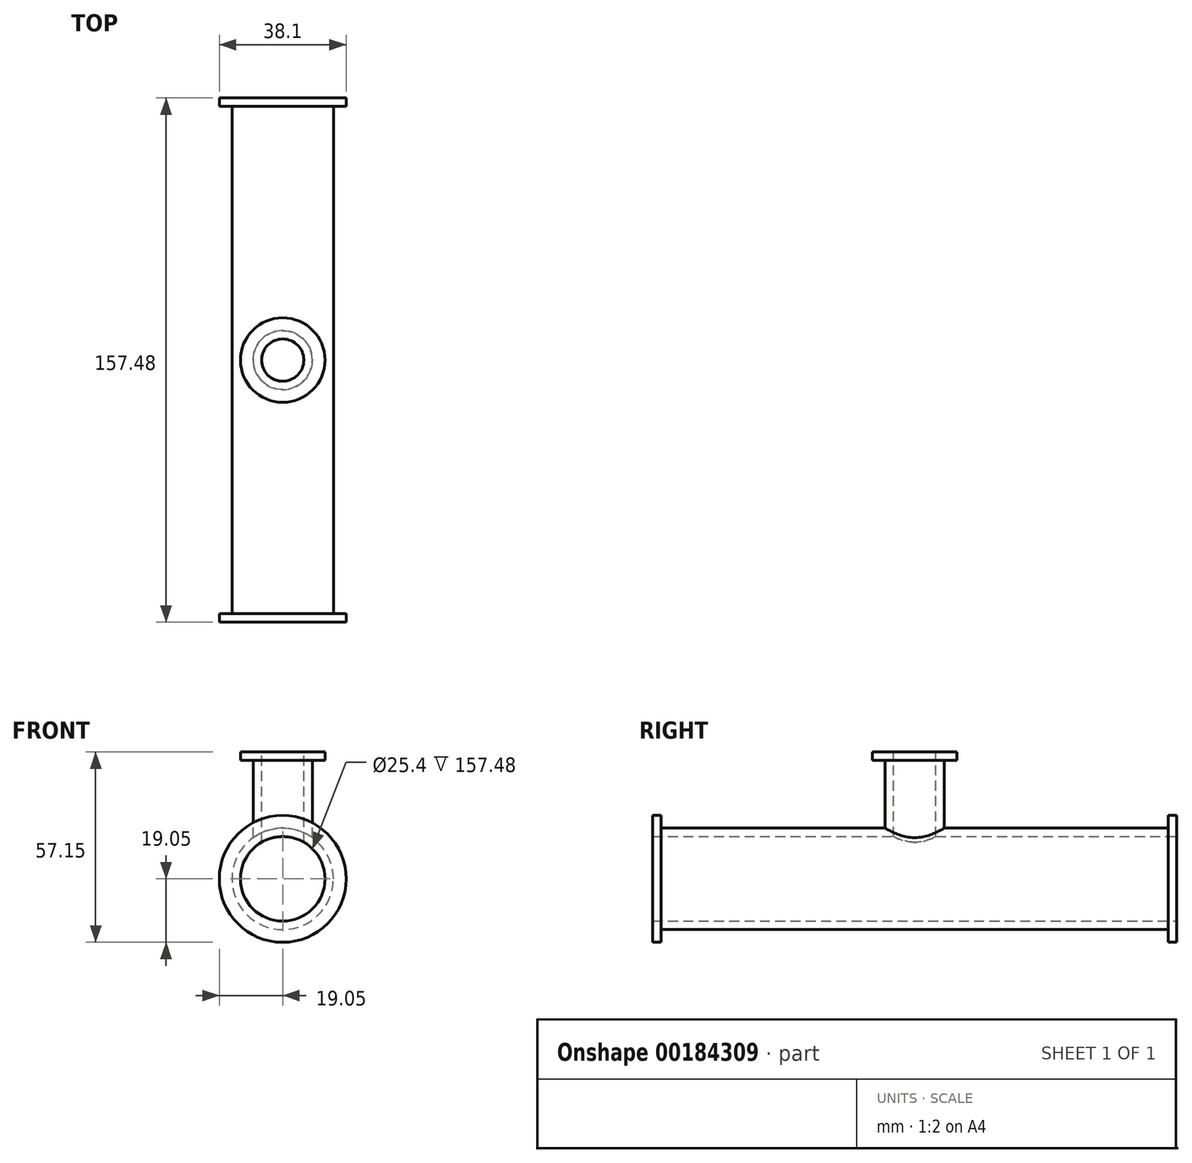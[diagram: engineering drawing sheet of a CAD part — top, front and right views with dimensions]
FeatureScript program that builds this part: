
annotation { "Feature Type Name" : "Feature", "Feature Type Description" : "" }
export const myFeature = defineFeature(function(context is Context, id is Id, definition is map)
    precondition{}
    {
        {
            var Q0;
            Q0=qCreatedBy(makeId("Front.planeOp"),FACE);
            var sketch = newSketch(context, id + "F0", { "sketchPlane" : qUnion([Q0])});
            skCircle(sketch, "E0", {"center": v(0, 0) * mm, "radius": 19.05 * mm});
            skCircle(sketch, "E1", {"center": v(0, 0) * mm, "radius": 12.7 * mm});
            skCircle(sketch, "E2", {"center": v(0, 0) * mm, "radius": 15.24 * mm});
            skSolve(sketch);
        }
        {
            var Q0;
            Q0=makeQuery(id+"F0.imprint","IMPRINT",FACE,{"disambiguationData":[TD([[makeQuery(id+"F0.imprint","IMPRINT",EDGE,{"derivedFrom":sQuery(id+"F0.wireOp",EDGE,"E1")}),-1.0]])]});
            extrude(context, id + "F1", {"entities" : qUnion([Q0]), "depth" : 157.48 * mm});
        }
        {
            var Q0;
            Q0=makeQuery(id+"F0.imprint","IMPRINT",FACE,{"disambiguationData":[TD([[makeQuery(id+"F0.imprint","IMPRINT",EDGE,{"derivedFrom":sQuery(id+"F0.wireOp",EDGE,"E0")}),1.0]])]});
            extrude(context, id + "F2", {"entities" : qUnion([Q0]), "operationType" : NewBodyOperationType.ADD, "depth" : 2.54 * mm});
        }
        {
            var Q0;
            Q0=makeQuery(id+"F1.opExtrude","CAP_FACE",FACE,{"disambiguationData":[OSD([sQuery(id+"F0.wireOp",EDGE,"E1"),sQuery(id+"F0.wireOp",EDGE,"E2")])],"isStart":false});
            var sketch = newSketch(context, id + "F3", { "sketchPlane" : qUnion([Q0])});
            skCircle(sketch, "E3", {"center": v(0, 0) * mm, "radius": 15.24 * mm});
            skCircle(sketch, "E4", {"center": v(0, 0) * mm, "radius": 19.05 * mm});
            skSolve(sketch);
        }
        {
            var Q0;
            Q0=qSketchRegion(id+"F3",true);
            extrude(context, id + "F4", {"entities" : qUnion([Q0]), "operationType" : NewBodyOperationType.ADD, "oppositeDirection" : true, "depth" : 2.54 * mm});
        }
        {
            var Q0;
            Q0=qCreatedBy(makeId("Top.planeOp"),FACE);
            cPlane(context, id + "F5", {"entities" : qUnion([Q0]), "cplaneType" : CPlaneType.OFFSET, "offset" : 25.4 * mm, "width" : 152.4 * mm, "height" : 152.4 * mm});
        }
        {
            var Q0;
            Q0=qCreatedBy(id+"F5.planeOp",FACE);
            var sketch = newSketch(context, id + "F6", { "sketchPlane" : qUnion([Q0])});
            skLineSegment(sketch, "E5", {"start": v(0, -2.54) * mm, "end": v(0, -78.74) * mm, "construction": true});
            skCircle(sketch, "E6", {"center": v(0, -78.74) * mm, "radius": 12.7 * mm});
            skCircle(sketch, "E7", {"center": v(0, -78.74) * mm, "radius": 8.9 * mm});
            skCircle(sketch, "E8", {"center": v(0, -78.74) * mm, "radius": 6.35 * mm});
            skSolve(sketch);
        }
        {
            var Q0;
            Q0=makeQuery(id+"F6.imprint","IMPRINT",FACE,{"disambiguationData":[TD([[makeQuery(id+"F6.imprint","IMPRINT",EDGE,{"derivedFrom":sQuery(id+"F6.wireOp",EDGE,"E7")}),1.0]])]});
            extrude(context, id + "F7", {"entities" : qUnion([Q0]), "operationType" : NewBodyOperationType.ADD, "oppositeDirection" : true, "depth" : 25.4 * mm, "hasSecondDirection" : true, "secondDirectionOppositeDirection" : false, "secondDirectionDepth" : 12.7 * mm});
        }
        {
            var Q0;
            Q0=makeQuery(id+"F7.opExtrude","CAP_FACE",FACE,{"disambiguationData":[OSD([sQuery(id+"F6.wireOp",EDGE,"E7"),sQuery(id+"F6.wireOp",EDGE,"E8")])],"isStart":true});
            var sketch = newSketch(context, id + "F8", { "sketchPlane" : qUnion([Q0])});
            skCircle(sketch, "E9", {"center": v(0, -78.74) * mm, "radius": 8.9 * mm});
            skCircle(sketch, "E10", {"center": v(0, -78.74) * mm, "radius": 12.7 * mm});
            skSolve(sketch);
        }
        {
            var Q0;
            Q0=qSketchRegion(id+"F8",true);
            extrude(context, id + "F9", {"entities" : qUnion([Q0]), "operationType" : NewBodyOperationType.ADD, "oppositeDirection" : true, "depth" : 2.54 * mm});
        }
        {
            var Q0;
            Q0=makeQuery(id+"F0.imprint","IMPRINT",FACE,{"disambiguationData":[TD([[makeQuery(id+"F0.imprint","IMPRINT",EDGE,{"derivedFrom":sQuery(id+"F0.wireOp",EDGE,"E1")}),1.0]])]});
            extrude(context, id + "F10", {"entities" : qUnion([Q0]), "operationType" : NewBodyOperationType.REMOVE, "depth" : 101.6 * mm});
        }
        {
            var Q0;
            Q0=makeQuery(id+"F8.imprint","IMPRINT",FACE,{"disambiguationData":[TD([[makeQuery(id+"F8.imprint","IMPRINT",EDGE,{"derivedFrom":makeQuery(id+"F7.opExtrude","CAP_EDGE",EDGE,{"disambiguationData":[OSD([sQuery(id+"F6.wireOp",EDGE,"E8")])],"isStart":true})}),1.0]])]});
            extrude(context, id + "F11", {"entities" : qUnion([Q0]), "operationType" : NewBodyOperationType.REMOVE, "oppositeDirection" : true, "depth" : 38.1 * mm});
        }
    });
